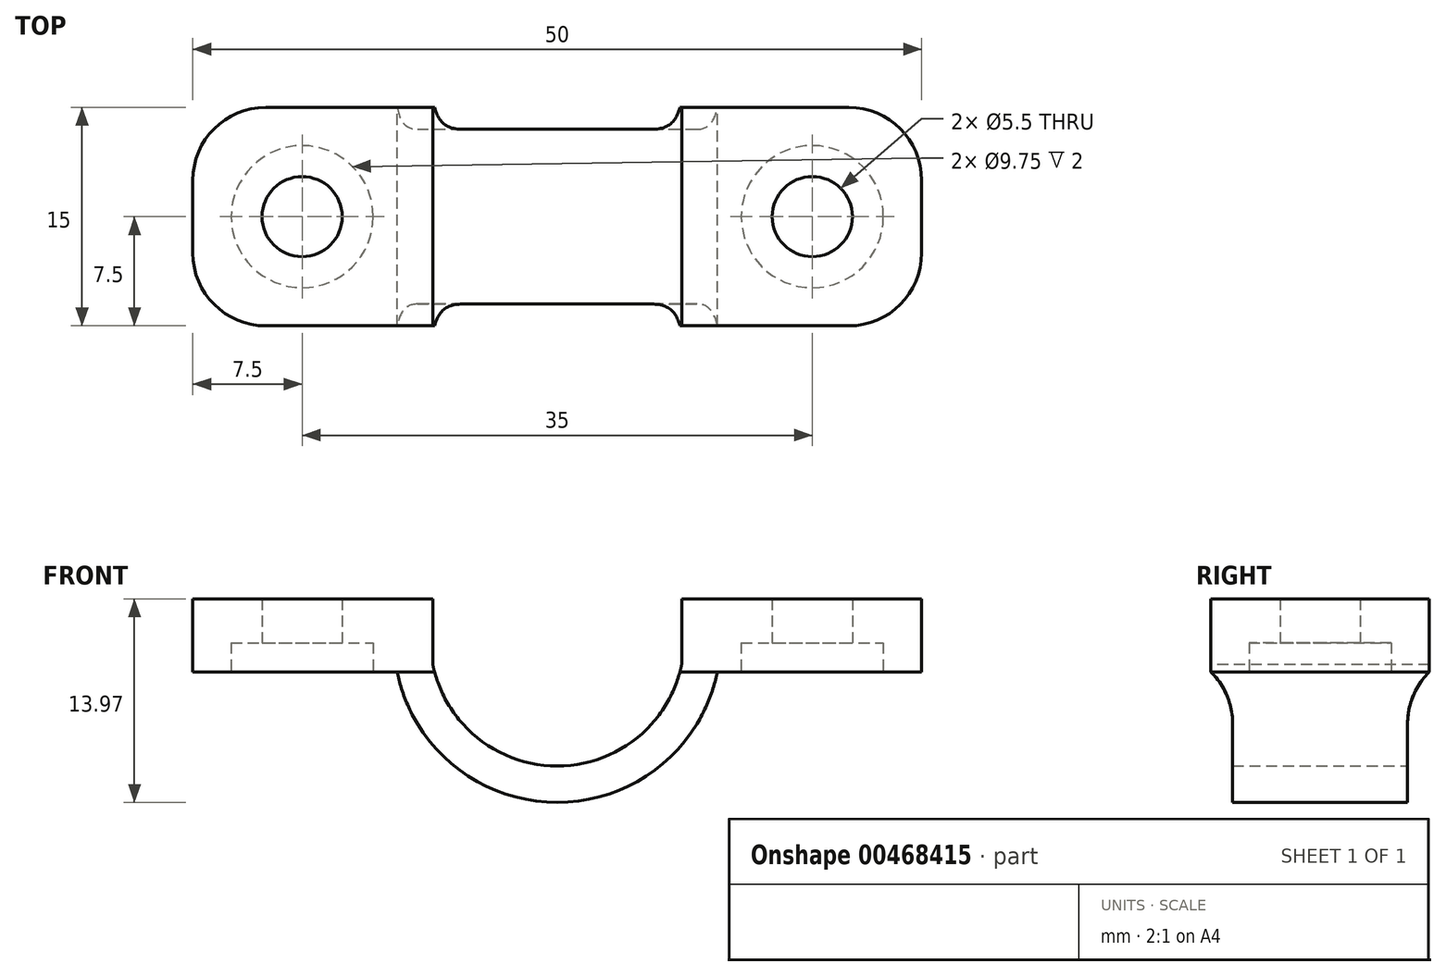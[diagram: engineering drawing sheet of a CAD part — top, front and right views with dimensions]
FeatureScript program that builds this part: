
annotation { "Feature Type Name" : "Feature", "Feature Type Description" : "" }
export const myFeature = defineFeature(function(context is Context, id is Id, definition is map)
    precondition{}
    {
        {
            var Q0;
            Q0=qCreatedBy(makeId("Top.planeOp"),FACE);
            var sketch = newSketch(context, id + "F0", { "sketchPlane" : qUnion([Q0])});
            skLineSegment(sketch, "E0.bottom", {"start": v(25, 7.5) * mm, "end": v(-25, 7.5) * mm});
            skLineSegment(sketch, "E0.top", {"start": v(25, -7.5) * mm, "end": v(-25, -7.5) * mm});
            skLineSegment(sketch, "E0.left", {"start": v(25, 7.5) * mm, "end": v(25, -7.5) * mm});
            skLineSegment(sketch, "E0.right", {"start": v(-25, 7.5) * mm, "end": v(-25, -7.5) * mm});
            skPoint(sketch, "E0.middle", {"position": v(0, 0) * mm});
            skLineSegment(sketch, "E1", {"start": v(-17.5, 0) * mm, "end": v(17.5, 0) * mm, "construction": true});
            skSolve(sketch);
        }
        {
            var Q0;
            Q0=makeQuery(id+"F0.imprint","IMPRINT",FACE,{"disambiguationData":[TD([[makeQuery(id+"F0.imprint","IMPRINT",EDGE,{"derivedFrom":sQuery(id+"F0.wireOp",EDGE,"E0.bottom")}),1.0]])]});
            extrude(context, id + "F1", {"entities" : qUnion([Q0]), "depth" : 5 * mm});
        }
        {
            var Q0;
            Q0=sQuery(id+"F0.wireOp",VERTEX,"E1.start");
            var Q1;
            Q1=sQuery(id+"F0.wireOp",VERTEX,"E1.end");
            var Q2;
            Q2=makeQuery(id+"F1.opExtrude","SWEPT_BODY",BODY,{"disambiguationData":[OSD([sQuery(id+"F0.wireOp",EDGE,"E0.bottom"),sQuery(id+"F0.wireOp",EDGE,"E0.top"),sQuery(id+"F0.wireOp",EDGE,"E0.left"),sQuery(id+"F0.wireOp",EDGE,"E0.right")])]});
            hole(context, id + "F2", {"style" : HoleStyle.C_BORE, "endStyle" : HoleEndStyle.BLIND, "oppositeDirection" : true, "holeDiameter" : 5.5 * mm, "cBoreDiameter" : 9.75 * mm, "cBoreDepth" : 2 * mm, "holeDepth" : 15 * mm, "isTappedThrough" : true, "tappedDepth" : 12 * mm, "tapClearance" : 3, "startFromSketch" : true, "locations" : qUnion([Q0, Q1]), "scope" : qUnion([Q2])});
        }
        {
            var Q0;
            Q0=qCreatedBy(makeId("Front.planeOp"),FACE);
            var sketch = newSketch(context, id + "F3", { "sketchPlane" : qUnion([Q0])});
            skArc(sketch, "E2", {"start": v(-10.98, 0) * mm, "mid": v(0, -8.97) * mm, "end": v(10.98, 0) * mm});
            skArc(sketch, "E3.0", {"start": v(-8.54, 0.5) * mm, "mid": v(0, -6.47) * mm, "end": v(8.54, 0.5) * mm});
            skLineSegment(sketch, "E4", {"start": v(-10.98, 0) * mm, "end": v(-8.54, 0.5) * mm});
            skLineSegment(sketch, "E5", {"start": v(8.54, 0.5) * mm, "end": v(10.98, 0) * mm});
            skLineSegment(sketch, "E6", {"start": v(-8.54, 0.5) * mm, "end": v(-8.54, 8.26) * mm});
            skLineSegment(sketch, "E7", {"start": v(-8.54, 8.26) * mm, "end": v(8.54, 8.26) * mm});
            skLineSegment(sketch, "E8", {"start": v(8.54, 8.26) * mm, "end": v(8.54, 0.5) * mm});
            skSolve(sketch);
        }
        {
            var Q0;
            Q0=makeQuery(id+"F3.imprint","IMPRINT",FACE,{"disambiguationData":[TD([[makeQuery(id+"F3.imprint","IMPRINT",EDGE,{"derivedFrom":sQuery(id+"F3.wireOp",EDGE,"E2")}),1.0]])]});
            extrude(context, id + "F4", {"entities" : qUnion([Q0]), "operationType" : NewBodyOperationType.ADD, "depth" : 6 * mm, "hasSecondDirection" : true, "secondDirectionOppositeDirection" : true, "secondDirectionDepth" : 6 * mm});
        }
        {
            var Q0;
            Q0=makeQuery(id+"F4.opExtrude","SWEPT_EDGE",EDGE,{"disambiguationData":[OSD([sQuery(id+"F3.wireOp",EDGE,"E2"),sQuery(id+"F3.wireOp",EDGE,"E4")])]});
            var Q1;
            Q1=makeQuery(id+"F4.opExtrude","SWEPT_EDGE",EDGE,{"disambiguationData":[OSD([sQuery(id+"F3.wireOp",EDGE,"E2"),sQuery(id+"F3.wireOp",EDGE,"E5")])]});
            var Q2;
            Q2=makeQuery(id+"F1.opExtrude","SWEPT_EDGE",EDGE,{"disambiguationData":[OSD([sQuery(id+"F0.wireOp",EDGE,"E0.bottom"),sQuery(id+"F0.wireOp",EDGE,"E0.left")])]});
            var Q3;
            Q3=makeQuery(id+"F1.opExtrude","SWEPT_EDGE",EDGE,{"disambiguationData":[OSD([sQuery(id+"F0.wireOp",EDGE,"E0.top"),sQuery(id+"F0.wireOp",EDGE,"E0.left")])]});
            var Q4;
            Q4=makeQuery(id+"F1.opExtrude","SWEPT_EDGE",EDGE,{"disambiguationData":[OSD([sQuery(id+"F0.wireOp",EDGE,"E0.bottom"),sQuery(id+"F0.wireOp",EDGE,"E0.right")])]});
            var Q5;
            Q5=makeQuery(id+"F1.opExtrude","SWEPT_EDGE",EDGE,{"disambiguationData":[OSD([sQuery(id+"F0.wireOp",EDGE,"E0.top"),sQuery(id+"F0.wireOp",EDGE,"E0.right")])]});
            fillet(context, id + "F5", {"entities" : qUnion([Q0, Q1, Q2, Q3, Q4, Q5]), "radius" : 5 * mm, "tangentPropagation" : true, "allowEdgeOverflow" : false});
        }
        {
            var Q0;
            Q0=makeQuery(id+"F3.imprint","IMPRINT",FACE,{"disambiguationData":[TD([[makeQuery(id+"F3.imprint","IMPRINT",EDGE,{"derivedFrom":sQuery(id+"F3.wireOp",EDGE,"E3.0")}),1.0]])]});
            extrude(context, id + "F6", {"entities" : qUnion([Q0]), "operationType" : NewBodyOperationType.REMOVE, "oppositeDirection" : true, "depth" : 25 * mm, "hasSecondDirection" : true, "secondDirectionOppositeDirection" : false, "secondDirectionDepth" : 25 * mm});
        }
        {
            var Q0;
            Q0=makeQuery(id+"F4.boolean.opBoolean","INTERSECT",EDGE,{"disambiguationData":[OD(0.0)],"derivedFrom":[makeQuery(id+"F1.opExtrude","CAP_FACE",FACE,{"disambiguationData":[OSD([sQuery(id+"F0.wireOp",EDGE,"E0.bottom"),sQuery(id+"F0.wireOp",EDGE,"E0.top"),sQuery(id+"F0.wireOp",EDGE,"E0.left"),sQuery(id+"F0.wireOp",EDGE,"E0.right")])],"isStart":true}),makeQuery(id+"F4.opExtrude","CAP_FACE",FACE,{"disambiguationData":[OSD([sQuery(id+"F3.wireOp",EDGE,"E2"),sQuery(id+"F3.wireOp",EDGE,"E3.0"),sQuery(id+"F3.wireOp",EDGE,"E4"),sQuery(id+"F3.wireOp",EDGE,"E5")])],"isStart":true})]});
            var Q1;
            Q1=makeQuery(id+"F4.boolean.opBoolean","INTERSECT",EDGE,{"disambiguationData":[OD(1.0)],"derivedFrom":[makeQuery(id+"F1.opExtrude","CAP_FACE",FACE,{"disambiguationData":[OSD([sQuery(id+"F0.wireOp",EDGE,"E0.bottom"),sQuery(id+"F0.wireOp",EDGE,"E0.top"),sQuery(id+"F0.wireOp",EDGE,"E0.left"),sQuery(id+"F0.wireOp",EDGE,"E0.right")])],"isStart":true}),makeQuery(id+"F4.opExtrude","CAP_FACE",FACE,{"disambiguationData":[OSD([sQuery(id+"F3.wireOp",EDGE,"E2"),sQuery(id+"F3.wireOp",EDGE,"E3.0"),sQuery(id+"F3.wireOp",EDGE,"E4"),sQuery(id+"F3.wireOp",EDGE,"E5")])],"isStart":true})]});
            var Q2;
            Q2=makeQuery(id+"F4.boolean.opBoolean","INTERSECT",EDGE,{"disambiguationData":[OD(1.0)],"derivedFrom":[makeQuery(id+"F1.opExtrude","CAP_FACE",FACE,{"disambiguationData":[OSD([sQuery(id+"F0.wireOp",EDGE,"E0.bottom"),sQuery(id+"F0.wireOp",EDGE,"E0.top"),sQuery(id+"F0.wireOp",EDGE,"E0.left"),sQuery(id+"F0.wireOp",EDGE,"E0.right")])],"isStart":true}),makeQuery(id+"F4.opExtrude","CAP_FACE",FACE,{"disambiguationData":[OSD([sQuery(id+"F3.wireOp",EDGE,"E2"),sQuery(id+"F3.wireOp",EDGE,"E3.0"),sQuery(id+"F3.wireOp",EDGE,"E4"),sQuery(id+"F3.wireOp",EDGE,"E5")])],"isStart":false})]});
            var Q3;
            Q3=makeQuery(id+"F4.boolean.opBoolean","INTERSECT",EDGE,{"disambiguationData":[OD(0.0)],"derivedFrom":[makeQuery(id+"F1.opExtrude","CAP_FACE",FACE,{"disambiguationData":[OSD([sQuery(id+"F0.wireOp",EDGE,"E0.bottom"),sQuery(id+"F0.wireOp",EDGE,"E0.top"),sQuery(id+"F0.wireOp",EDGE,"E0.left"),sQuery(id+"F0.wireOp",EDGE,"E0.right")])],"isStart":true}),makeQuery(id+"F4.opExtrude","CAP_FACE",FACE,{"disambiguationData":[OSD([sQuery(id+"F3.wireOp",EDGE,"E2"),sQuery(id+"F3.wireOp",EDGE,"E3.0"),sQuery(id+"F3.wireOp",EDGE,"E4"),sQuery(id+"F3.wireOp",EDGE,"E5")])],"isStart":false})]});
            fillet(context, id + "F7", {"entities" : qUnion([Q0, Q1, Q2, Q3]), "radius" : 5 * mm, "tangentPropagation" : true, "allowEdgeOverflow" : false});
        }
    });
